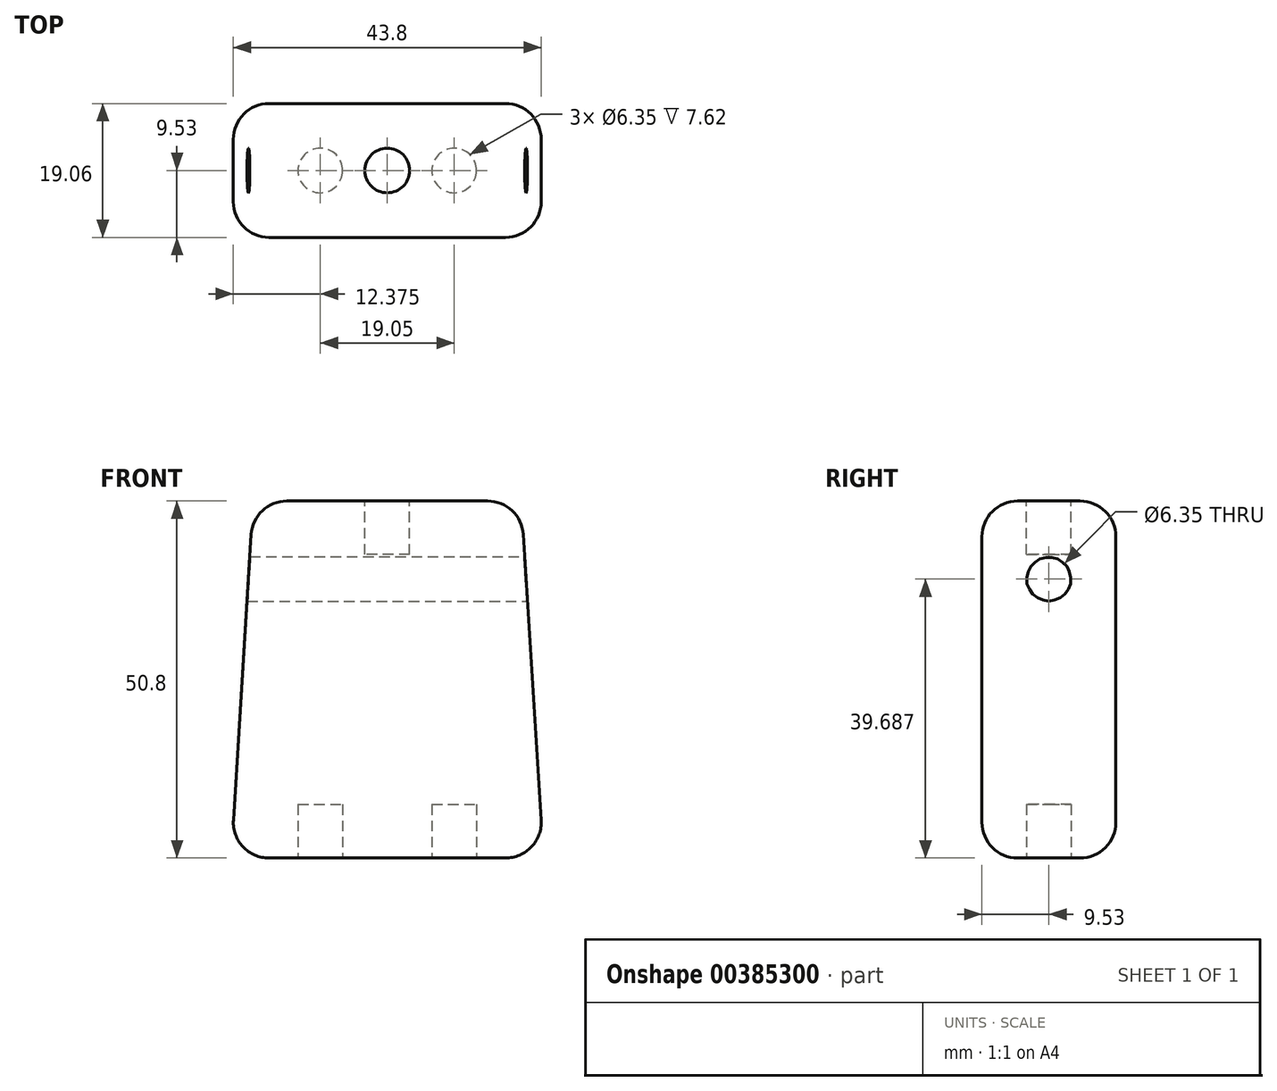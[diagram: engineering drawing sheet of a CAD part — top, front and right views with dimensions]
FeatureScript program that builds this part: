
annotation { "Feature Type Name" : "Feature", "Feature Type Description" : "" }
export const myFeature = defineFeature(function(context is Context, id is Id, definition is map)
    precondition{}
    {
        {
            var Q0;
            Q0=qCreatedBy(makeId("Front.planeOp"),FACE);
            var sketch = newSketch(context, id + "F0", { "sketchPlane" : qUnion([Q0])});
            skLineSegment(sketch, "E0.bottom", {"start": v(-22.23, 0) * mm, "end": v(22.23, 0) * mm});
            skLineSegment(sketch, "E0.top", {"start": v(-19.05, 50.8) * mm, "end": v(19.05, 50.8) * mm});
            skLineSegment(sketch, "E1", {"start": v(-22.23, 0) * mm, "end": v(-19.05, 50.8) * mm});
            skLineSegment(sketch, "E2", {"start": v(22.23, 0) * mm, "end": v(19.05, 50.8) * mm});
            skLineSegment(sketch, "E3", {"start": v(0, 0) * mm, "end": v(0, 50.8) * mm, "construction": true});
            skSolve(sketch);
        }
        {
            var Q0;
            Q0 = qSketchRegion(id + "F0", true);
            extrude(context, id + "F1", {"entities" : qUnion([Q0]), "endBound" : BoundingType.SYMMETRIC, "depth" : 19.05 * mm});
        }
        {
            var Q0;
            Q0=makeQuery(id+"F1.opExtrude","CAP_EDGE",EDGE,{"disambiguationData":[OSD([sQuery(id+"F0.wireOp",EDGE,"E0.top")])],"isStart":false});
            var Q1;
            Q1=makeQuery(id+"F1.opExtrude","SWEPT_EDGE",EDGE,{"disambiguationData":[OSD([sQuery(id+"F0.wireOp",EDGE,"E0.top"),sQuery(id+"F0.wireOp",EDGE,"E2")])]});
            var Q2;
            Q2=makeQuery(id+"F1.opExtrude","SWEPT_EDGE",EDGE,{"disambiguationData":[OSD([sQuery(id+"F0.wireOp",EDGE,"E0.top"),sQuery(id+"F0.wireOp",EDGE,"E1")])]});
            var Q3;
            Q3=makeQuery(id+"F1.opExtrude","CAP_EDGE",EDGE,{"disambiguationData":[OSD([sQuery(id+"F0.wireOp",EDGE,"E0.top")])],"isStart":true});
            var Q4;
            Q4=makeQuery(id+"F1.opExtrude","SWEPT_EDGE",EDGE,{"disambiguationData":[OSD([sQuery(id+"F0.wireOp",EDGE,"E0.bottom"),sQuery(id+"F0.wireOp",EDGE,"E2")])]});
            var Q5;
            Q5=makeQuery(id+"F1.opExtrude","CAP_EDGE",EDGE,{"disambiguationData":[OSD([sQuery(id+"F0.wireOp",EDGE,"E0.bottom")])],"isStart":false});
            var Q6;
            Q6=makeQuery(id+"F1.opExtrude","SWEPT_EDGE",EDGE,{"disambiguationData":[OSD([sQuery(id+"F0.wireOp",EDGE,"E0.bottom"),sQuery(id+"F0.wireOp",EDGE,"E1")])]});
            var Q7;
            Q7=makeQuery(id+"F1.opExtrude","CAP_EDGE",EDGE,{"disambiguationData":[OSD([sQuery(id+"F0.wireOp",EDGE,"E0.bottom")])],"isStart":true});
            var Q8;
            Q8=makeQuery(id+"F1.opExtrude","CAP_EDGE",EDGE,{"disambiguationData":[OSD([sQuery(id+"F0.wireOp",EDGE,"E2")])],"isStart":false});
            var Q9;
            Q9=makeQuery(id+"F1.opExtrude","CAP_EDGE",EDGE,{"disambiguationData":[OSD([sQuery(id+"F0.wireOp",EDGE,"E2")])],"isStart":true});
            var Q10;
            Q10=makeQuery(id+"F1.opExtrude","CAP_EDGE",EDGE,{"disambiguationData":[OSD([sQuery(id+"F0.wireOp",EDGE,"E1")])],"isStart":true});
            var Q11;
            Q11=makeQuery(id+"F1.opExtrude","SWEPT_FACE",FACE,{"disambiguationData":[OSD([sQuery(id+"F0.wireOp",EDGE,"E1")])]});
            fillet(context, id + "F2", {"entities" : qUnion([Q0, Q1, Q2, Q3, Q4, Q5, Q6, Q7, Q8, Q9, Q10, Q11]), "radius" : 5.08 * mm, "tangentPropagation" : true, "allowEdgeOverflow" : false});
        }
        {
            var Q0;
            Q0=qCreatedBy(makeId("Right.planeOp"),FACE);
            var sketch = newSketch(context, id + "F3", { "sketchPlane" : qUnion([Q0])});
            skCircle(sketch, "E4", {"center": v(0, 39.69) * mm, "radius": 3.18 * mm});
            skSolve(sketch);
        }
        {
            var Q0;
            Q0 = qSketchRegion(id + "F3", true);
            extrude(context, id + "F4", {"entities" : qUnion([Q0]), "operationType" : NewBodyOperationType.REMOVE, "endBound" : BoundingType.SYMMETRIC, "oppositeDirection" : true, "depth" : 50.8 * mm});
        }
        {
            var Q0;
            Q0=makeQuery(id+"F1.opExtrude","SWEPT_FACE",FACE,{"disambiguationData":[OSD([sQuery(id+"F0.wireOp",EDGE,"E0.top")])]});
            var sketch = newSketch(context, id + "F5", { "sketchPlane" : qUnion([Q0])});
            skCircle(sketch, "E5", {"center": v(0, 0) * mm, "radius": 3.18 * mm});
            skSolve(sketch);
        }
        {
            var Q0;
            Q0 = qSketchRegion(id + "F5", true);
            extrude(context, id + "F6", {"entities" : qUnion([Q0]), "operationType" : NewBodyOperationType.REMOVE, "oppositeDirection" : true, "depth" : 7.62 * mm});
        }
        {
            var Q0;
            Q0=makeQuery(id+"F1.opExtrude","SWEPT_FACE",FACE,{"disambiguationData":[OSD([sQuery(id+"F0.wireOp",EDGE,"E0.bottom")])]});
            var sketch = newSketch(context, id + "F7", { "sketchPlane" : qUnion([Q0])});
            skCircle(sketch, "E6", {"center": v(-9.53, 0) * mm, "radius": 3.18 * mm});
            skCircle(sketch, "E7", {"center": v(9.53, 0) * mm, "radius": 3.17 * mm});
            skLineSegment(sketch, "E8", {"start": v(-9.52, 0) * mm, "end": v(9.53, 0) * mm, "construction": true});
            skSolve(sketch);
        }
        {
            var Q0;
            Q0 = qSketchRegion(id + "F7", true);
            extrude(context, id + "F8", {"entities" : qUnion([Q0]), "operationType" : NewBodyOperationType.REMOVE, "oppositeDirection" : true, "depth" : 7.62 * mm});
        }
    });
